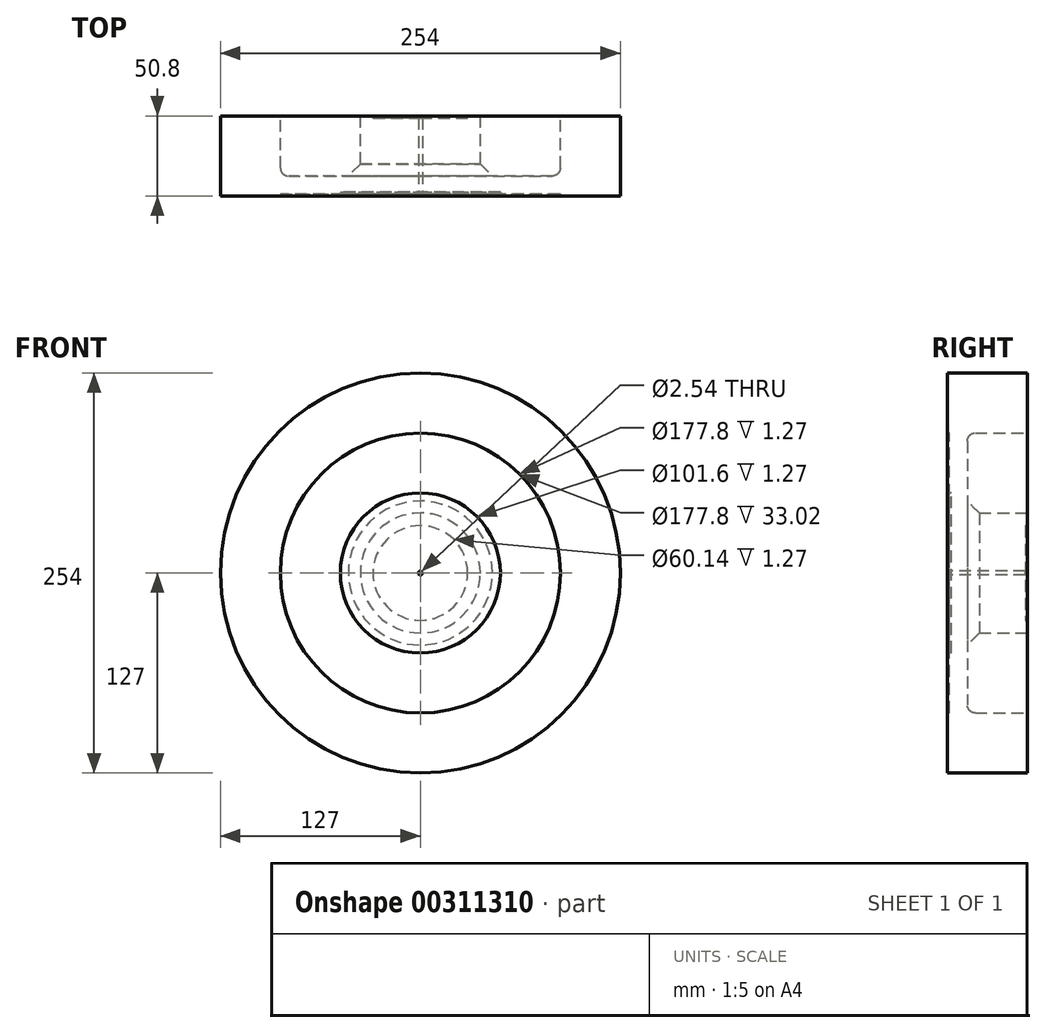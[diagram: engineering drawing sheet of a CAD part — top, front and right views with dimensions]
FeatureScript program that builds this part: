
annotation { "Feature Type Name" : "Feature", "Feature Type Description" : "" }
export const myFeature = defineFeature(function(context is Context, id is Id, definition is map)
    precondition{}
    {
        {
            var Q0;
            Q0=qCreatedBy(makeId("Front.planeOp"),FACE);
            var sketch = newSketch(context, id + "F0", { "sketchPlane" : qUnion([Q0])});
            skCircle(sketch, "E0", {"center": v(0, 0) * mm, "radius": 127 * mm});
            skSolve(sketch);
        }
        {
            var Q0;
            Q0 = qSketchRegion(id + "F0", true);
            extrude(context, id + "F1", {"entities" : qUnion([Q0]), "depth" : 50.8 * mm});
        }
        {
            var Q0;
            Q0=makeQuery(id+"F1.opExtrude","CAP_FACE",FACE,{"disambiguationData":[OSD([sQuery(id+"F0.wireOp",EDGE,"E0")])],"isStart":false});
            var sketch = newSketch(context, id + "F2", { "sketchPlane" : qUnion([Q0])});
            skCircle(sketch, "E1", {"center": v(0, 0) * mm, "radius": 88.9 * mm});
            skSolve(sketch);
        }
        {
            var Q0;
            Q0 = qSketchRegion(id + "F2", true);
            extrude(context, id + "F3", {"entities" : qUnion([Q0]), "operationType" : NewBodyOperationType.REMOVE, "oppositeDirection" : true, "depth" : 1.27 * mm});
        }
        {
            var Q0;
            Q0=makeQuery(id+"F3.boolean.opBoolean","COPY",FACE,{"derivedFrom":makeQuery(id+"F3.opExtrude","CAP_FACE",FACE,{"disambiguationData":[OSD([sQuery(id+"F2.wireOp",EDGE,"E1")])],"isStart":false})});
            var sketch = newSketch(context, id + "F4", { "sketchPlane" : qUnion([Q0])});
            skCircle(sketch, "E2", {"center": v(0, 0) * mm, "radius": 1.27 * mm});
            skPoint(sketch, "E3.center.orphan", {"position": v(3.56, 0) * mm});
            skSolve(sketch);
        }
        {
            var Q0;
            Q0 = qSketchRegion(id + "F4", true);
            extrude(context, id + "F5", {"entities" : qUnion([Q0]), "operationType" : NewBodyOperationType.REMOVE, "oppositeDirection" : true, "depth" : 50.8 * mm});
        }
        {
            var Q0;
            Q0=makeQuery(id+"F3.boolean.opBoolean","COPY",FACE,{"derivedFrom":makeQuery(id+"F3.opExtrude","CAP_FACE",FACE,{"disambiguationData":[OSD([sQuery(id+"F2.wireOp",EDGE,"E1")])],"isStart":false})});
            var sketch = newSketch(context, id + "F6", { "sketchPlane" : qUnion([Q0])});
            skCircle(sketch, "E4", {"center": v(0, 0) * mm, "radius": 50.8 * mm});
            skSolve(sketch);
        }
        {
            var Q0;
            Q0 = qSketchRegion(id + "F6", true);
            extrude(context, id + "F7", {"entities" : qUnion([Q0]), "operationType" : NewBodyOperationType.REMOVE, "oppositeDirection" : true, "depth" : 1.27 * mm});
        }
        {
            var Q0;
            Q0=makeQuery(id+"F1.opExtrude","CAP_FACE",FACE,{"disambiguationData":[OSD([sQuery(id+"F0.wireOp",EDGE,"E0")])],"isStart":true});
            var sketch = newSketch(context, id + "F8", { "sketchPlane" : qUnion([Q0])});
            skCircle(sketch, "E5.0", {"center": v(0, 0) * mm, "radius": 88.9 * mm});
            skCircle(sketch, "E6", {"center": v(0, 0) * mm, "radius": 38.1 * mm});
            skSolve(sketch);
        }
        {
            var Q0;
            Q0 = qSketchRegion(id + "F8", true);
            extrude(context, id + "F9", {"entities" : qUnion([Q0]), "operationType" : NewBodyOperationType.REMOVE, "oppositeDirection" : true, "depth" : 38.1 * mm});
        }
        {
            var Q0;
            Q0=makeQuery(id+"F9.boolean.opBoolean","COPY",EDGE,{"derivedFrom":makeQuery(id+"F9.opExtrude","CAP_EDGE",EDGE,{"disambiguationData":[OSD([sQuery(id+"F8.wireOp",EDGE,"E6")])],"isStart":false})});
            chamfer(context, id + "F10", {"entities" : qUnion([Q0]), "width" : 7.62 * mm, "tangentPropagation" : true});
        }
        {
            var Q0;
            Q0=makeQuery(id+"F9.boolean.opBoolean","COPY",EDGE,{"derivedFrom":makeQuery(id+"F9.opExtrude","CAP_EDGE",EDGE,{"disambiguationData":[OSD([sQuery(id+"F8.wireOp",EDGE,"E5.0")])],"isStart":false})});
            fillet(context, id + "F11", {"entities" : qUnion([Q0]), "radius" : 5.08 * mm, "tangentPropagation" : true, "allowEdgeOverflow" : false});
        }
        {
            var Q0;
            Q0=makeQuery(id+"F1.opExtrude","CAP_FACE",FACE,{"disambiguationData":[OSD([sQuery(id+"F0.wireOp",EDGE,"E0")])],"isStart":false});
            var sketch = newSketch(context, id + "F12", { "sketchPlane" : qUnion([Q0])});
            skLineSegment(sketch, "E7", {"start": v(0, 127) * mm, "end": v(0, 107.95) * mm, "construction": true});
            skArc(sketch, "E8.0", {"start": v(3, 107.9) * mm, "mid": v(0, 107.95) * mm, "end": v(-3, 107.9) * mm});
            skLineSegment(sketch, "E9.0", {"start": v(-9.53, 127) * mm, "end": v(-9.53, 114.26) * mm});
            skLineSegment(sketch, "E10.0", {"start": v(9.53, 127) * mm, "end": v(9.53, 114.26) * mm});
            skPoint(sketch, "E11.visualSharp", {"position": v(-9.52, 107.53) * mm});
            skArc(sketch, "E11.filletArc", {"start": v(-9.53, 114.26) * mm, "mid": v(-7.6, 109.7) * mm, "end": v(-3, 107.9) * mm});
            skPoint(sketch, "E12.visualSharp", {"position": v(9.53, 107.53) * mm});
            skArc(sketch, "E12.filletArc", {"start": v(3, 107.9) * mm, "mid": v(7.6, 109.7) * mm, "end": v(9.53, 114.26) * mm});
            skLineSegment(sketch, "E13", {"start": v(-9.53, 117.47) * mm, "end": v(9.53, 117.47) * mm, "construction": true});
            skPoint(sketch, "E13.startSnap0", {"position": v(0, 117.47) * mm});
            skArc(sketch, "E14.0", {"start": v(9.52, 126.64) * mm, "mid": v(0, 127) * mm, "end": v(-9.52, 126.64) * mm});
            skArc(sketch, "E15.1.0", {"start": v(-82.81, 96.28) * mm, "mid": v(-89.8, 89.8) * mm, "end": v(-96.28, 82.81) * mm});
            skLineSegment(sketch, "E15.1.1", {"start": v(-83.07, 96.54) * mm, "end": v(-74.06, 87.53) * mm});
            skArc(sketch, "E15.1.2", {"start": v(-74.18, 78.42) * mm, "mid": v(-72.2, 82.95) * mm, "end": v(-74.06, 87.53) * mm});
            skArc(sketch, "E15.1.3", {"start": v(-74.18, 78.42) * mm, "mid": v(-76.33, 76.33) * mm, "end": v(-78.42, 74.18) * mm});
            skArc(sketch, "E15.1.4", {"start": v(-87.53, 74.06) * mm, "mid": v(-82.95, 72.2) * mm, "end": v(-78.42, 74.18) * mm});
            skLineSegment(sketch, "E15.1.5", {"start": v(-96.54, 83.07) * mm, "end": v(-87.53, 74.06) * mm});
            skArc(sketch, "E15.2.0", {"start": v(-126.64, 9.52) * mm, "mid": v(-127, 0) * mm, "end": v(-126.64, -9.52) * mm});
            skLineSegment(sketch, "E15.2.1", {"start": v(-127, 9.53) * mm, "end": v(-114.26, 9.53) * mm});
            skArc(sketch, "E15.2.2", {"start": v(-107.9, 3) * mm, "mid": v(-109.7, 7.6) * mm, "end": v(-114.26, 9.53) * mm});
            skArc(sketch, "E15.2.3", {"start": v(-107.9, 3) * mm, "mid": v(-107.95, 0) * mm, "end": v(-107.9, -3) * mm});
            skArc(sketch, "E15.2.4", {"start": v(-114.26, -9.52) * mm, "mid": v(-109.7, -7.6) * mm, "end": v(-107.9, -3) * mm});
            skLineSegment(sketch, "E15.2.5", {"start": v(-127, -9.52) * mm, "end": v(-114.26, -9.52) * mm});
            skArc(sketch, "E15.3.0", {"start": v(-96.28, -82.81) * mm, "mid": v(-89.8, -89.8) * mm, "end": v(-82.81, -96.28) * mm});
            skLineSegment(sketch, "E15.3.1", {"start": v(-96.54, -83.07) * mm, "end": v(-87.53, -74.06) * mm});
            skArc(sketch, "E15.3.2", {"start": v(-78.42, -74.18) * mm, "mid": v(-82.95, -72.2) * mm, "end": v(-87.53, -74.06) * mm});
            skArc(sketch, "E15.3.3", {"start": v(-78.42, -74.18) * mm, "mid": v(-76.33, -76.33) * mm, "end": v(-74.18, -78.42) * mm});
            skArc(sketch, "E15.3.4", {"start": v(-74.06, -87.53) * mm, "mid": v(-72.2, -82.95) * mm, "end": v(-74.18, -78.42) * mm});
            skLineSegment(sketch, "E15.3.5", {"start": v(-83.07, -96.54) * mm, "end": v(-74.06, -87.53) * mm});
            skArc(sketch, "E15.4.0", {"start": v(-9.53, -126.64) * mm, "mid": v(0, -127) * mm, "end": v(9.52, -126.64) * mm});
            skLineSegment(sketch, "E15.4.1", {"start": v(-9.53, -127) * mm, "end": v(-9.53, -114.26) * mm});
            skArc(sketch, "E15.4.2", {"start": v(-3, -107.9) * mm, "mid": v(-7.6, -109.7) * mm, "end": v(-9.53, -114.26) * mm});
            skArc(sketch, "E15.4.3", {"start": v(-3, -107.9) * mm, "mid": v(0, -107.95) * mm, "end": v(3, -107.9) * mm});
            skArc(sketch, "E15.4.4", {"start": v(9.52, -114.26) * mm, "mid": v(7.6, -109.7) * mm, "end": v(3, -107.9) * mm});
            skLineSegment(sketch, "E15.4.5", {"start": v(9.52, -127) * mm, "end": v(9.52, -114.26) * mm});
            skArc(sketch, "E15.5.0", {"start": v(82.81, -96.28) * mm, "mid": v(89.8, -89.8) * mm, "end": v(96.28, -82.81) * mm});
            skLineSegment(sketch, "E15.5.1", {"start": v(83.07, -96.54) * mm, "end": v(74.06, -87.53) * mm});
            skArc(sketch, "E15.5.2", {"start": v(74.18, -78.42) * mm, "mid": v(72.2, -82.95) * mm, "end": v(74.06, -87.53) * mm});
            skArc(sketch, "E15.5.3", {"start": v(74.18, -78.42) * mm, "mid": v(76.33, -76.33) * mm, "end": v(78.42, -74.18) * mm});
            skArc(sketch, "E15.5.4", {"start": v(87.53, -74.06) * mm, "mid": v(82.95, -72.2) * mm, "end": v(78.42, -74.18) * mm});
            skLineSegment(sketch, "E15.5.5", {"start": v(96.54, -83.07) * mm, "end": v(87.53, -74.06) * mm});
            skArc(sketch, "E15.6.0", {"start": v(126.64, -9.53) * mm, "mid": v(127, 0) * mm, "end": v(126.64, 9.52) * mm});
            skLineSegment(sketch, "E15.6.1", {"start": v(127, -9.53) * mm, "end": v(114.26, -9.53) * mm});
            skArc(sketch, "E15.6.2", {"start": v(107.9, -3) * mm, "mid": v(109.7, -7.6) * mm, "end": v(114.26, -9.53) * mm});
            skArc(sketch, "E15.6.3", {"start": v(107.9, -3) * mm, "mid": v(107.95, 0) * mm, "end": v(107.9, 3) * mm});
            skArc(sketch, "E15.6.4", {"start": v(114.26, 9.52) * mm, "mid": v(109.7, 7.6) * mm, "end": v(107.9, 3) * mm});
            skLineSegment(sketch, "E15.6.5", {"start": v(127, 9.52) * mm, "end": v(114.26, 9.52) * mm});
            skArc(sketch, "E15.7.0", {"start": v(96.28, 82.81) * mm, "mid": v(89.8, 89.8) * mm, "end": v(82.81, 96.28) * mm});
            skLineSegment(sketch, "E15.7.1", {"start": v(96.54, 83.07) * mm, "end": v(87.53, 74.06) * mm});
            skArc(sketch, "E15.7.2", {"start": v(78.42, 74.18) * mm, "mid": v(82.95, 72.2) * mm, "end": v(87.53, 74.06) * mm});
            skArc(sketch, "E15.7.3", {"start": v(78.42, 74.18) * mm, "mid": v(76.33, 76.33) * mm, "end": v(74.18, 78.42) * mm});
            skArc(sketch, "E15.7.4", {"start": v(74.06, 87.53) * mm, "mid": v(72.2, 82.95) * mm, "end": v(74.18, 78.42) * mm});
            skLineSegment(sketch, "E15.7.5", {"start": v(83.07, 96.54) * mm, "end": v(74.06, 87.53) * mm});
            skSolve(sketch);
        }
        {
            var Q0;
            Q0 = qSketchRegion(id + "F12", true);
            extrude(context, id + "F13", {"entities" : qUnion([Q0]), "operationType" : NewBodyOperationType.ADD, "oppositeDirection" : true, "depth" : 44.45 * mm});
        }
        {
            var Q0;
            Q0=makeQuery(id+"F9.boolean.opBoolean","SPLIT",FACE,{"disambiguationData":[TD([makeQuery(id+"F5.boolean.opBoolean","COPY",FACE,{"derivedFrom":makeQuery(id+"F5.opExtrude","SWEPT_FACE",FACE,{"disambiguationData":[OSD([sQuery(id+"F4.wireOp",EDGE,"E2")])]})})])],"derivedFrom":makeQuery(id+"F1.opExtrude","CAP_FACE",FACE,{"disambiguationData":[OSD([sQuery(id+"F0.wireOp",EDGE,"E0")])],"isStart":true})});
            var sketch = newSketch(context, id + "F14", { "sketchPlane" : qUnion([Q0])});
            skCircle(sketch, "E16", {"center": v(0, 0) * mm, "radius": 30.07 * mm});
            skCircle(sketch, "E17.0", {"center": v(0, 0) * mm, "radius": 1.27 * mm});
            skSolve(sketch);
        }
        {
            var Q0;
            Q0 = qSketchRegion(id + "F14", true);
            extrude(context, id + "F15", {"entities" : qUnion([Q0]), "operationType" : NewBodyOperationType.REMOVE, "oppositeDirection" : true, "depth" : 1.27 * mm});
        }
    });
